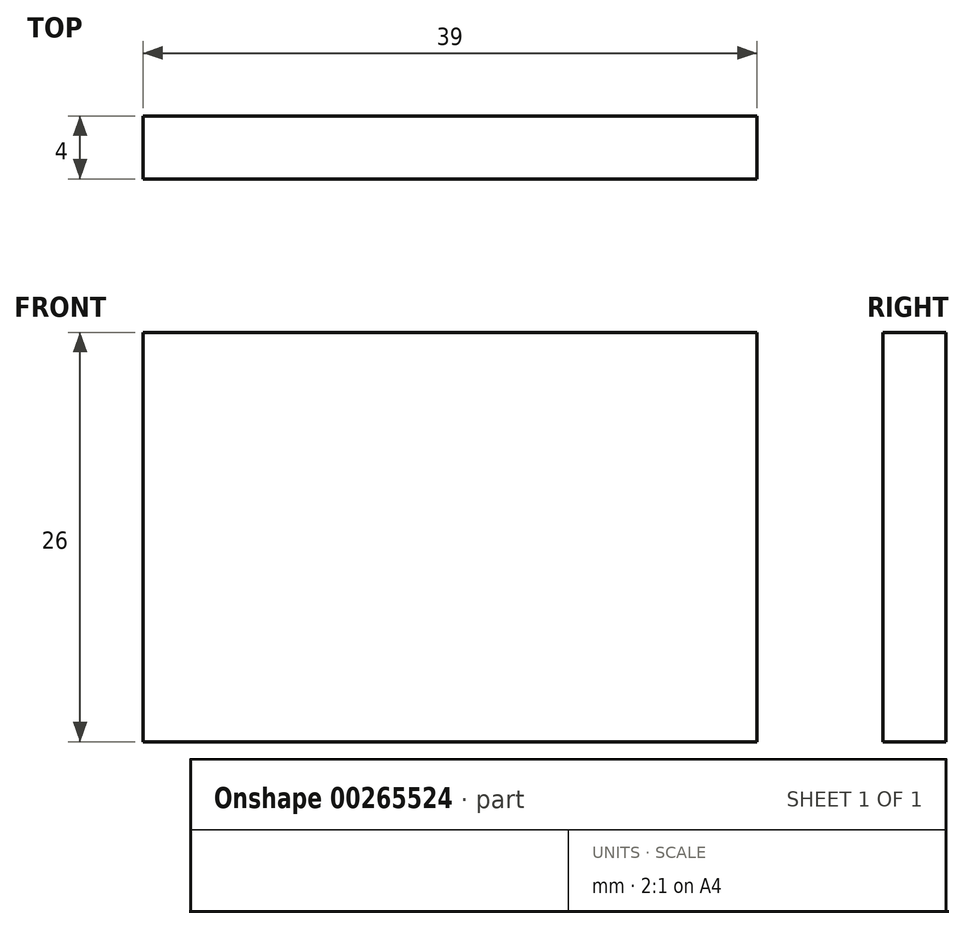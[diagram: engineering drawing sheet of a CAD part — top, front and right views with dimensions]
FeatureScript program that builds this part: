
annotation { "Feature Type Name" : "Feature", "Feature Type Description" : "" }
export const myFeature = defineFeature(function(context is Context, id is Id, definition is map)
    precondition{}
    {
        {
            var Q0;
            Q0=qCreatedBy(makeId("Front.planeOp"),FACE);
            var sketch = newSketch(context, id + "F0", { "sketchPlane" : qUnion([Q0])});
            skLineSegment(sketch, "E0.bottom", {"start": v(19.5, 13) * mm, "end": v(-19.5, 13) * mm});
            skLineSegment(sketch, "E0.top", {"start": v(19.5, -13) * mm, "end": v(-19.5, -13) * mm});
            skLineSegment(sketch, "E0.left", {"start": v(19.5, 13) * mm, "end": v(19.5, -13) * mm});
            skLineSegment(sketch, "E0.right", {"start": v(-19.5, 13) * mm, "end": v(-19.5, -13) * mm});
            skPoint(sketch, "E0.middle", {"position": v(0, 0) * mm});
            skSolve(sketch);
        }
        {
            var Q0;
            Q0 = qSketchRegion(id + "F0", true);
            extrude(context, id + "F1", {"entities" : qUnion([Q0]), "depth" : 4 * mm});
        }
    });
